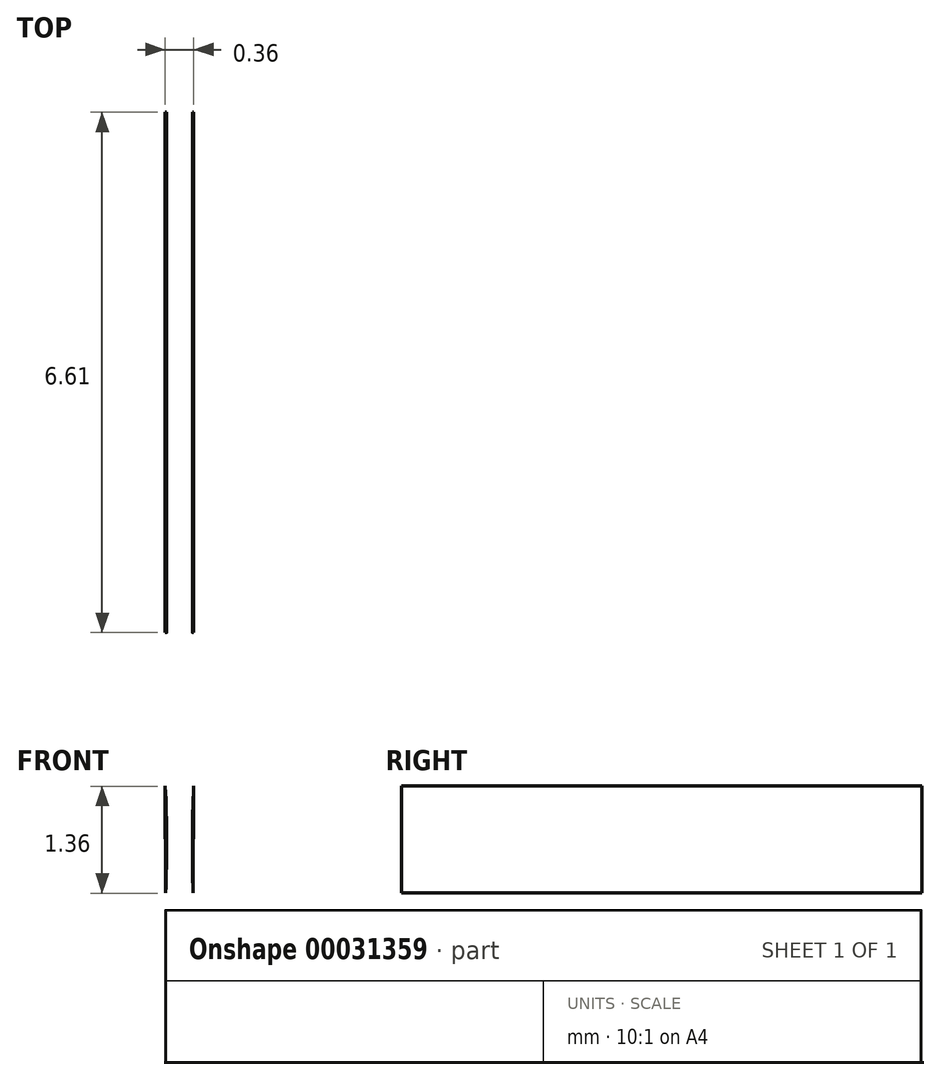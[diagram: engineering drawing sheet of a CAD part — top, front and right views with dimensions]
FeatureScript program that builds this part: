
annotation { "Feature Type Name" : "Feature", "Feature Type Description" : "" }
export const myFeature = defineFeature(function(context is Context, id is Id, definition is map)
    precondition{}
    {
        {
            var Q0;
            Q0=qCreatedBy(makeId("Front.planeOp"),FACE);
            var sketch = newSketch(context, id + "F0", { "sketchPlane" : qUnion([Q0])});
            skCircle(sketch, "E0", {"center": v(17.27, 17.18) * mm, "radius": 17.11 * mm});
            skLineSegment(sketch, "E1", {"start": v(0.18, 17.92) * mm, "end": v(0, -30.66) * mm});
            skLineSegment(sketch, "E2", {"start": v(0, -30.66) * mm, "end": v(31.73, 8.03) * mm});
            skSolve(sketch);
        }
        {
            var Q0;
            {var subQ1=sQuery(id+"F0.wireOp",EDGE,"E0");var subQ4=sQuery(id+"F0.wireOp",EDGE,"E1");var subQ5=makeQuery(id+"F0.imprint","INTERSECT",VERTEX,{"disambiguationData":[OD(1.0)],"derivedFrom":[subQ1,subQ4]});Q0=makeQuery(id+"F0.imprint","IMPRINT",FACE,{"disambiguationData":[TD([[makeQuery(id+"F0.imprint","IMPRINT",EDGE,{"disambiguationData":[TD([[subQ5,-1.0]])],"derivedFrom":subQ1}),1.0]])]});}
            var Q1;
            {var subQ1=sQuery(id+"F0.wireOp",EDGE,"E0");var subQ3=sQuery(id+"F0.wireOp",EDGE,"E1");var subQ5=makeQuery(id+"F0.imprint","INTERSECT",VERTEX,{"disambiguationData":[OD(1.0)],"derivedFrom":[subQ1,subQ3]});Q1=makeQuery(id+"F0.imprint","IMPRINT",FACE,{"disambiguationData":[TD([[makeQuery(id+"F0.imprint","IMPRINT",EDGE,{"disambiguationData":[TD([[subQ5,-1.0]])],"derivedFrom":subQ1}),-1.0]])]});}
            extrude(context, id + "F1", {"entities" : qUnion([Q0, Q1]), "depth" : 6.6 * mm});
        }
        {
            var Q0;
            Q0=makeQuery(id+"F1.opExtrude","SWEPT_BODY",BODY,{"disambiguationData":[OSD([sQuery(id+"F0.wireOp",EDGE,"E0"),sQuery(id+"F0.wireOp",EDGE,"E1"),sQuery(id+"F0.wireOp",EDGE,"E2")])]});
            var Q1;
            Q1=qCreatedBy(makeId("Right.planeOp"),FACE);
            mirror(context, id + "F2", {"entities" : qUnion([Q0]), "mirrorPlane" : qUnion([Q1])});
        }
    });
